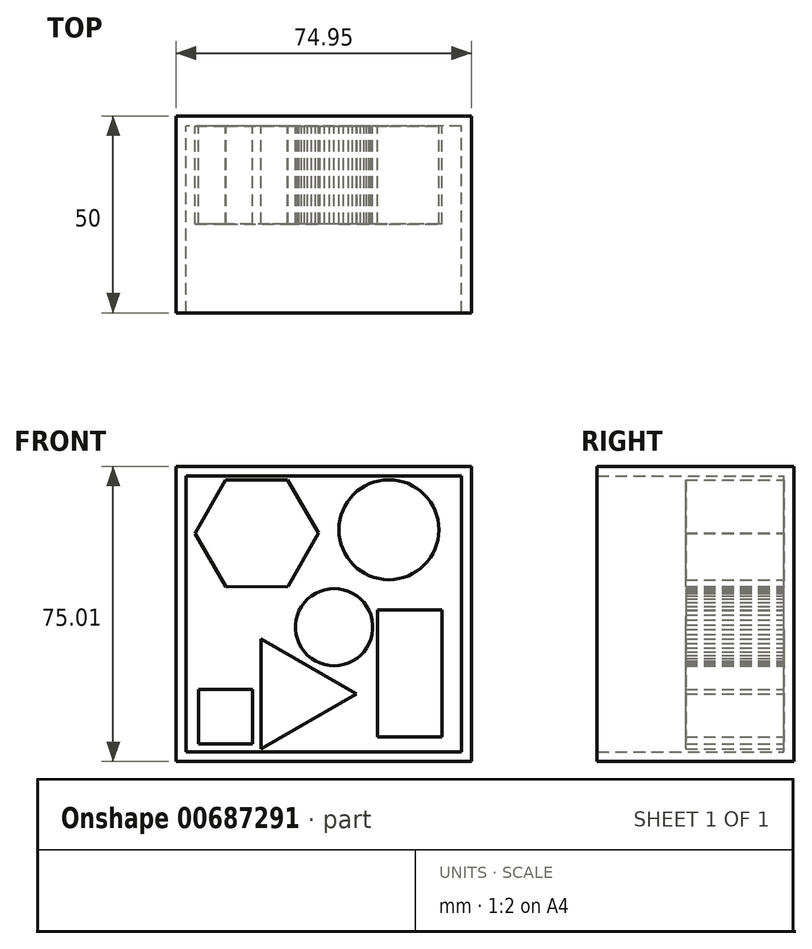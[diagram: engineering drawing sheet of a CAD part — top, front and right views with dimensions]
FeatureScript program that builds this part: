
annotation { "Feature Type Name" : "Feature", "Feature Type Description" : "" }
export const myFeature = defineFeature(function(context is Context, id is Id, definition is map)
    precondition{}
    {
        {
            var Q0;
            Q0=qCreatedBy(makeId("Front.planeOp"),FACE);
            var sketch = newSketch(context, id + "F0", { "sketchPlane" : qUnion([Q0])});
            skLineSegment(sketch, "E0.bottom", {"start": v(0, 0) * mm, "end": v(-74.95, 0) * mm});
            skLineSegment(sketch, "E0.top", {"start": v(0, 75) * mm, "end": v(-74.95, 75) * mm});
            skLineSegment(sketch, "E0.left", {"start": v(0, 0) * mm, "end": v(0, 75) * mm});
            skLineSegment(sketch, "E0.right", {"start": v(-74.95, 0) * mm, "end": v(-74.95, 75) * mm});
            skSolve(sketch);
        }
        {
            var Q0;
            Q0 = qSketchRegion(id + "F0", true);
            extrude(context, id + "F1", {"entities" : qUnion([Q0]), "depth" : 25 * mm, "offsetDistance" : 25 * mm});
        }
        {
            var Q0;
            Q0=makeQuery(id+"F1.opExtrude","CAP_FACE",FACE,{"disambiguationData":[OSD([sQuery(id+"F0.wireOp",EDGE,"E0.bottom"),sQuery(id+"F0.wireOp",EDGE,"E0.top"),sQuery(id+"F0.wireOp",EDGE,"E0.left"),sQuery(id+"F0.wireOp",EDGE,"E0.right")])],"isStart":true});
            extrude(context, id + "F2", {"entities" : qUnion([Q0]), "operationType" : NewBodyOperationType.ADD, "depth" : 25 * mm, "offsetDistance" : 25 * mm});
        }
        {
            var Q0;
            Q0=makeQuery(id+"F1.opExtrude","CAP_FACE",FACE,{"disambiguationData":[OSD([sQuery(id+"F0.wireOp",EDGE,"E0.bottom"),sQuery(id+"F0.wireOp",EDGE,"E0.top"),sQuery(id+"F0.wireOp",EDGE,"E0.left"),sQuery(id+"F0.wireOp",EDGE,"E0.right")])],"isStart":false});
            shell(context, id + "F3", {"entities" : qUnion([Q0]), "thickness" : 2.5 * mm});
        }
        {
            var Q0;
            Q0=makeQuery(id+"F3.opShell","OFFSET_FACE",FACE,{"disambiguationData":[OSD([sQuery(id+"F0.wireOp",EDGE,"E0.bottom"),sQuery(id+"F0.wireOp",EDGE,"E0.top"),sQuery(id+"F0.wireOp",EDGE,"E0.left"),sQuery(id+"F0.wireOp",EDGE,"E0.right")])]});
            var sketch = newSketch(context, id + "F4", { "sketchPlane" : qUnion([Q0])});
            skCircle(sketch, "E1.cCircle", {"center": v(-54.47, 57.95) * mm, "radius": 13.55 * mm, "construction": true});
            skLineSegment(sketch, "E1.0", {"start": v(-38.83, 58.03) * mm, "end": v(-46.59, 44.44) * mm});
            skLineSegment(sketch, "E1.1", {"start": v(-46.59, 44.44) * mm, "end": v(-62.23, 44.37) * mm});
            skLineSegment(sketch, "E1.2", {"start": v(-62.23, 44.37) * mm, "end": v(-70.12, 57.88) * mm});
            skLineSegment(sketch, "E1.3", {"start": v(-70.12, 57.88) * mm, "end": v(-62.36, 71.47) * mm});
            skLineSegment(sketch, "E1.4", {"start": v(-62.36, 71.47) * mm, "end": v(-46.71, 71.54) * mm});
            skLineSegment(sketch, "E1.5", {"start": v(-46.71, 71.54) * mm, "end": v(-38.83, 58.03) * mm});
            skPoint(sketch, "E1.0.midPoint", {"position": v(-42.7, 51.23) * mm});
            skSolve(sketch);
        }
        {
            var Q0;
            Q0 = qSketchRegion(id + "F4", true);
            extrude(context, id + "F5", {"entities" : qUnion([Q0]), "operationType" : NewBodyOperationType.ADD, "depth" : 25 * mm, "offsetDistance" : 25 * mm});
        }
        {
            var Q0;
            Q0=makeQuery(id+"F3.opShell","OFFSET_FACE",FACE,{"disambiguationData":[OSD([sQuery(id+"F0.wireOp",EDGE,"E0.bottom"),sQuery(id+"F0.wireOp",EDGE,"E0.top"),sQuery(id+"F0.wireOp",EDGE,"E0.left"),sQuery(id+"F0.wireOp",EDGE,"E0.right")])]});
            var sketch = newSketch(context, id + "F6", { "sketchPlane" : qUnion([Q0])});
            skCircle(sketch, "E2", {"center": v(-20.92, 58.89) * mm, "radius": 12.7 * mm});
            skSolve(sketch);
        }
        {
            var Q0;
            Q0 = qSketchRegion(id + "F6", true);
            extrude(context, id + "F7", {"entities" : qUnion([Q0]), "operationType" : NewBodyOperationType.ADD, "depth" : 25 * mm, "offsetDistance" : 25 * mm});
        }
        {
            var Q0;
            Q0=makeQuery(id+"F3.opShell","OFFSET_FACE",FACE,{"disambiguationData":[OSD([sQuery(id+"F0.wireOp",EDGE,"E0.bottom"),sQuery(id+"F0.wireOp",EDGE,"E0.top"),sQuery(id+"F0.wireOp",EDGE,"E0.left"),sQuery(id+"F0.wireOp",EDGE,"E0.right")])]});
            var sketch = newSketch(context, id + "F8", { "sketchPlane" : qUnion([Q0])});
            skLineSegment(sketch, "E3.bottom", {"start": v(-7.4, 6.27) * mm, "end": v(-23.85, 6.27) * mm});
            skLineSegment(sketch, "E3.top", {"start": v(-7.4, 38.54) * mm, "end": v(-23.85, 38.54) * mm});
            skLineSegment(sketch, "E3.left", {"start": v(-7.4, 6.27) * mm, "end": v(-7.4, 38.54) * mm});
            skLineSegment(sketch, "E3.right", {"start": v(-23.85, 6.27) * mm, "end": v(-23.85, 38.54) * mm});
            skSolve(sketch);
        }
        {
            var Q0;
            Q0 = qSketchRegion(id + "F8", true);
            extrude(context, id + "F9", {"entities" : qUnion([Q0]), "operationType" : NewBodyOperationType.ADD, "depth" : 25 * mm, "offsetDistance" : 25 * mm});
        }
        {
            var Q0;
            Q0=makeQuery(id+"F3.opShell","OFFSET_FACE",FACE,{"disambiguationData":[OSD([sQuery(id+"F0.wireOp",EDGE,"E0.bottom"),sQuery(id+"F0.wireOp",EDGE,"E0.top"),sQuery(id+"F0.wireOp",EDGE,"E0.left"),sQuery(id+"F0.wireOp",EDGE,"E0.right")])]});
            var sketch = newSketch(context, id + "F10", { "sketchPlane" : qUnion([Q0])});
            skCircle(sketch, "E4.cCircle", {"center": v(-45.3, 17.18) * mm, "radius": 8.1 * mm, "construction": true});
            skLineSegment(sketch, "E4.0", {"start": v(-53.4, 3.15) * mm, "end": v(-53.4, 31.2) * mm});
            skLineSegment(sketch, "E4.1", {"start": v(-53.4, 31.2) * mm, "end": v(-29.1, 17.18) * mm});
            skLineSegment(sketch, "E4.2", {"start": v(-29.1, 17.18) * mm, "end": v(-53.4, 3.15) * mm});
            skPoint(sketch, "E4.0.midPoint", {"position": v(-53.4, 17.18) * mm});
            skSolve(sketch);
        }
        {
            var Q0;
            Q0 = qSketchRegion(id + "F10", true);
            extrude(context, id + "F11", {"entities" : qUnion([Q0]), "operationType" : NewBodyOperationType.ADD, "depth" : 25 * mm, "offsetDistance" : 25 * mm});
        }
        {
            var Q0;
            Q0=makeQuery(id+"F3.opShell","OFFSET_FACE",FACE,{"disambiguationData":[OSD([sQuery(id+"F0.wireOp",EDGE,"E0.bottom"),sQuery(id+"F0.wireOp",EDGE,"E0.top"),sQuery(id+"F0.wireOp",EDGE,"E0.left"),sQuery(id+"F0.wireOp",EDGE,"E0.right")])]});
            var sketch = newSketch(context, id + "F12", { "sketchPlane" : qUnion([Q0])});
            skLineSegment(sketch, "E5.bottom", {"start": v(-55.54, 4.49) * mm, "end": v(-69.31, 4.49) * mm});
            skLineSegment(sketch, "E5.top", {"start": v(-55.54, 18.27) * mm, "end": v(-69.31, 18.27) * mm});
            skLineSegment(sketch, "E5.left", {"start": v(-55.54, 4.49) * mm, "end": v(-55.54, 18.27) * mm});
            skLineSegment(sketch, "E5.right", {"start": v(-69.31, 4.49) * mm, "end": v(-69.31, 18.27) * mm});
            skSolve(sketch);
        }
        {
            var Q0;
            Q0 = qSketchRegion(id + "F12", true);
            extrude(context, id + "F13", {"entities" : qUnion([Q0]), "operationType" : NewBodyOperationType.ADD, "depth" : 25 * mm, "offsetDistance" : 25 * mm});
        }
        {
            var Q0;
            Q0=makeQuery(id+"F3.opShell","OFFSET_FACE",FACE,{"disambiguationData":[OSD([sQuery(id+"F0.wireOp",EDGE,"E0.bottom"),sQuery(id+"F0.wireOp",EDGE,"E0.top"),sQuery(id+"F0.wireOp",EDGE,"E0.left"),sQuery(id+"F0.wireOp",EDGE,"E0.right")])]});
            var sketch = newSketch(context, id + "F14", { "sketchPlane" : qUnion([Q0])});
            skCircle(sketch, "E6.cCircle", {"center": v(-34.84, 34.15) * mm, "radius": 9.8 * mm, "construction": true});
            skLineSegment(sketch, "E6.0", {"start": v(-44.63, 33.53) * mm, "end": v(-44.63, 34.76) * mm});
            skLineSegment(sketch, "E6.1", {"start": v(-44.63, 34.76) * mm, "end": v(-44.48, 35.98) * mm});
            skLineSegment(sketch, "E6.2", {"start": v(-44.48, 35.98) * mm, "end": v(-44.17, 37.18) * mm});
            skLineSegment(sketch, "E6.3", {"start": v(-44.17, 37.18) * mm, "end": v(-43.72, 38.32) * mm});
            skLineSegment(sketch, "E6.4", {"start": v(-43.72, 38.32) * mm, "end": v(-43.12, 39.4) * mm});
            skLineSegment(sketch, "E6.5", {"start": v(-43.12, 39.4) * mm, "end": v(-42.4, 40.4) * mm});
            skLineSegment(sketch, "E6.6", {"start": v(-42.4, 40.4) * mm, "end": v(-41.55, 41.3) * mm});
            skLineSegment(sketch, "E6.7", {"start": v(-41.55, 41.3) * mm, "end": v(-40.6, 42.08) * mm});
            skLineSegment(sketch, "E6.8", {"start": v(-40.6, 42.08) * mm, "end": v(-39.56, 42.75) * mm});
            skLineSegment(sketch, "E6.9", {"start": v(-39.56, 42.75) * mm, "end": v(-38.45, 43.27) * mm});
            skLineSegment(sketch, "E6.10", {"start": v(-38.45, 43.27) * mm, "end": v(-37.28, 43.65) * mm});
            skLineSegment(sketch, "E6.11", {"start": v(-37.28, 43.65) * mm, "end": v(-36.07, 43.88) * mm});
            skLineSegment(sketch, "E6.12", {"start": v(-36.07, 43.88) * mm, "end": v(-34.84, 43.96) * mm});
            skLineSegment(sketch, "E6.13", {"start": v(-34.84, 43.96) * mm, "end": v(-33.6, 43.88) * mm});
            skLineSegment(sketch, "E6.14", {"start": v(-33.6, 43.88) * mm, "end": v(-32.4, 43.65) * mm});
            skLineSegment(sketch, "E6.15", {"start": v(-32.4, 43.65) * mm, "end": v(-31.22, 43.27) * mm});
            skLineSegment(sketch, "E6.16", {"start": v(-31.22, 43.27) * mm, "end": v(-30.1, 42.75) * mm});
            skLineSegment(sketch, "E6.17", {"start": v(-30.1, 42.75) * mm, "end": v(-29.07, 42.08) * mm});
            skLineSegment(sketch, "E6.18", {"start": v(-29.07, 42.08) * mm, "end": v(-28.12, 41.3) * mm});
            skLineSegment(sketch, "E6.19", {"start": v(-28.12, 41.3) * mm, "end": v(-27.28, 40.4) * mm});
            skLineSegment(sketch, "E6.20", {"start": v(-27.28, 40.4) * mm, "end": v(-26.55, 39.4) * mm});
            skLineSegment(sketch, "E6.21", {"start": v(-26.55, 39.4) * mm, "end": v(-25.96, 38.32) * mm});
            skLineSegment(sketch, "E6.22", {"start": v(-25.96, 38.32) * mm, "end": v(-25.5, 37.18) * mm});
            skLineSegment(sketch, "E6.23", {"start": v(-25.5, 37.18) * mm, "end": v(-25.2, 35.98) * mm});
            skLineSegment(sketch, "E6.24", {"start": v(-25.2, 35.98) * mm, "end": v(-25.04, 34.76) * mm});
            skLineSegment(sketch, "E6.25", {"start": v(-25.04, 34.76) * mm, "end": v(-25.04, 33.53) * mm});
            skLineSegment(sketch, "E6.26", {"start": v(-25.04, 33.53) * mm, "end": v(-25.2, 32.3) * mm});
            skLineSegment(sketch, "E6.27", {"start": v(-25.2, 32.3) * mm, "end": v(-25.5, 31.11) * mm});
            skLineSegment(sketch, "E6.28", {"start": v(-25.5, 31.11) * mm, "end": v(-25.96, 29.97) * mm});
            skLineSegment(sketch, "E6.29", {"start": v(-25.96, 29.97) * mm, "end": v(-26.55, 28.89) * mm});
            skLineSegment(sketch, "E6.30", {"start": v(-26.55, 28.89) * mm, "end": v(-27.28, 27.9) * mm});
            skLineSegment(sketch, "E6.31", {"start": v(-27.28, 27.9) * mm, "end": v(-28.12, 27) * mm});
            skLineSegment(sketch, "E6.32", {"start": v(-28.12, 27) * mm, "end": v(-29.07, 26.2) * mm});
            skLineSegment(sketch, "E6.33", {"start": v(-29.07, 26.2) * mm, "end": v(-30.1, 25.55) * mm});
            skLineSegment(sketch, "E6.34", {"start": v(-30.1, 25.55) * mm, "end": v(-31.22, 25.02) * mm});
            skLineSegment(sketch, "E6.35", {"start": v(-31.22, 25.02) * mm, "end": v(-32.4, 24.64) * mm});
            skLineSegment(sketch, "E6.36", {"start": v(-32.4, 24.64) * mm, "end": v(-33.6, 24.41) * mm});
            skLineSegment(sketch, "E6.37", {"start": v(-33.6, 24.41) * mm, "end": v(-34.84, 24.33) * mm});
            skLineSegment(sketch, "E6.38", {"start": v(-34.84, 24.33) * mm, "end": v(-36.07, 24.41) * mm});
            skLineSegment(sketch, "E6.39", {"start": v(-36.07, 24.41) * mm, "end": v(-37.28, 24.64) * mm});
            skLineSegment(sketch, "E6.40", {"start": v(-37.28, 24.64) * mm, "end": v(-38.45, 25.02) * mm});
            skLineSegment(sketch, "E6.41", {"start": v(-38.45, 25.02) * mm, "end": v(-39.56, 25.55) * mm});
            skLineSegment(sketch, "E6.42", {"start": v(-39.56, 25.55) * mm, "end": v(-40.6, 26.2) * mm});
            skLineSegment(sketch, "E6.43", {"start": v(-40.6, 26.2) * mm, "end": v(-41.55, 27) * mm});
            skLineSegment(sketch, "E6.44", {"start": v(-41.55, 27) * mm, "end": v(-42.4, 27.9) * mm});
            skLineSegment(sketch, "E6.45", {"start": v(-42.4, 27.9) * mm, "end": v(-43.12, 28.89) * mm});
            skLineSegment(sketch, "E6.46", {"start": v(-43.12, 28.89) * mm, "end": v(-43.72, 29.97) * mm});
            skLineSegment(sketch, "E6.47", {"start": v(-43.72, 29.97) * mm, "end": v(-44.17, 31.11) * mm});
            skLineSegment(sketch, "E6.48", {"start": v(-44.17, 31.11) * mm, "end": v(-44.48, 32.3) * mm});
            skLineSegment(sketch, "E6.49", {"start": v(-44.48, 32.3) * mm, "end": v(-44.63, 33.53) * mm});
            skPoint(sketch, "E6.0.midPoint", {"position": v(-44.63, 34.15) * mm});
            skSolve(sketch);
        }
        {
            var Q0;
            Q0 = qSketchRegion(id + "F14", true);
            extrude(context, id + "F15", {"entities" : qUnion([Q0]), "operationType" : NewBodyOperationType.ADD, "depth" : 25 * mm, "offsetDistance" : 25 * mm});
        }
    });
